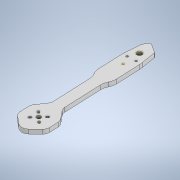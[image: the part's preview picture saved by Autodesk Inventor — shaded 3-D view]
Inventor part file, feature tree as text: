
AUTODESK INVENTOR PART (.ipt)
format: ipt  version: 2020 (Build 240168000, 168)  size: 170,496 bytes
history: native  units: mm
features: other x2, sketch x1
ambient origin geometry x8: Origin, YZ Plane, XZ Plane, XY Plane, X Axis, Y Axis, Z Axis, Center Point
bodies: Solid1 (feature_tree)
feature tree (3):
  other  "froggy arm assm.iam"
  other  "og kauri arm.ipt:1"
  sketch  "Sketch2"  dims[d0=10.0mm]
